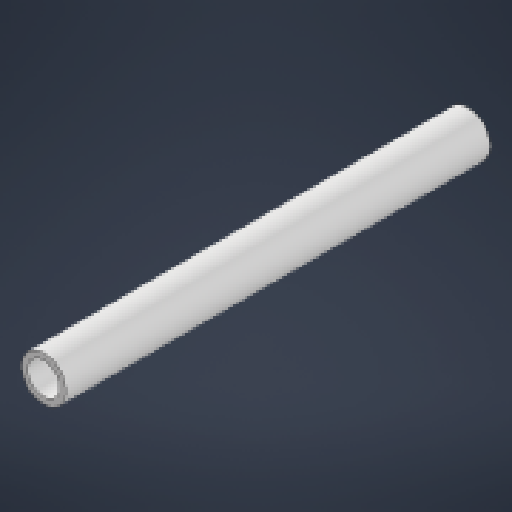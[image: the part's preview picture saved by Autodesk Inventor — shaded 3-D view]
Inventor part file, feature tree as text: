
AUTODESK INVENTOR PART (.ipt)
format: ipt  version: 2024.1 (Build 281209000, 209)  size: 124,928 bytes
history: native  units: in
note: dims shown in document units (in); Inventor stores cm internally (conversion verified against a paired STEP export)
features: extrude x1, sketch x1
ambient origin geometry x8: Origin, YZ Plane, XZ Plane, XY Plane, X Axis, Y Axis, Z Axis, Center Point
bodies: Solid1 (feature_tree)
feature tree (2):
  extrude  "Extrusion1"  Depth=8.0in
  sketch  "Sketch1"  dims[d0=0.84in d1=0.602in d2=8.0in d3=0.0in]
